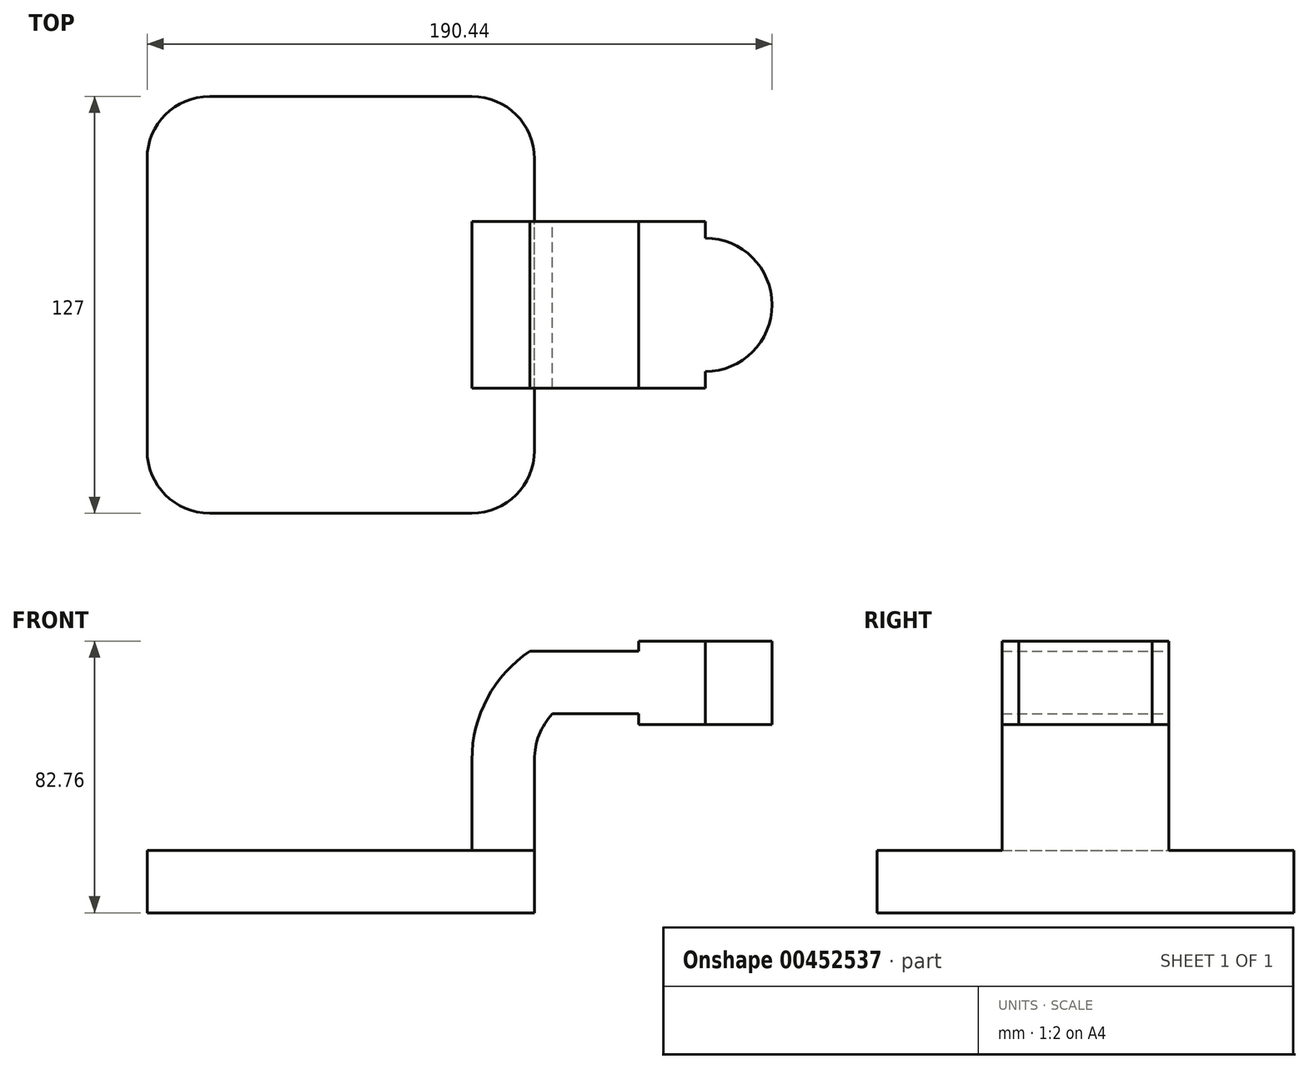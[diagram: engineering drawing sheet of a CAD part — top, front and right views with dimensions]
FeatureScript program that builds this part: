
annotation { "Feature Type Name" : "Feature", "Feature Type Description" : "" }
export const myFeature = defineFeature(function(context is Context, id is Id, definition is map)
    precondition{}
    {
        {
            var Q0;
            Q0=qCreatedBy(makeId("Front.planeOp"),FACE);
            var sketch = newSketch(context, id + "F0", { "sketchPlane" : qUnion([Q0])});
            skLineSegment(sketch, "E0.bottom", {"start": v(59.02, -9.52) * mm, "end": v(-59.02, -9.53) * mm});
            skLineSegment(sketch, "E0.top", {"start": v(59.02, 9.53) * mm, "end": v(-59.02, 9.53) * mm});
            skLineSegment(sketch, "E0.left", {"start": v(59.02, -9.52) * mm, "end": v(59.02, 9.53) * mm});
            skLineSegment(sketch, "E0.right", {"start": v(-59.02, -9.53) * mm, "end": v(-59.02, 9.53) * mm});
            skPoint(sketch, "E0.middle", {"position": v(0, 0) * mm});
            skLineSegment(sketch, "E1.bottom", {"start": v(131.42, 47.83) * mm, "end": v(90.78, 47.83) * mm});
            skLineSegment(sketch, "E1.top", {"start": v(131.42, 73.23) * mm, "end": v(90.78, 73.23) * mm});
            skLineSegment(sketch, "E1.left", {"start": v(131.42, 47.83) * mm, "end": v(131.42, 73.23) * mm});
            skLineSegment(sketch, "E1.right", {"start": v(90.78, 47.83) * mm, "end": v(90.78, 73.23) * mm});
            skPoint(sketch, "E1.middle", {"position": v(111.1, 60.53) * mm});
            skLineSegment(sketch, "E2", {"start": v(59.02, 9.53) * mm, "end": v(59.02, 37.13) * mm});
            skArc(sketch, "E3", {"start": v(59.02, 37.13) * mm, "mid": v(60.44, 44.63) * mm, "end": v(64.48, 51.1) * mm});
            skLineSegment(sketch, "E4", {"start": v(64.48, 51.1) * mm, "end": v(110.03, 51.1) * mm});
            skLineSegment(sketch, "E5.0", {"start": v(57.68, 70.15) * mm, "end": v(110.03, 70.15) * mm});
            skArc(sketch, "E5.1", {"start": v(39.97, 37.13) * mm, "mid": v(44.68, 55.87) * mm, "end": v(57.68, 70.15) * mm});
            skLineSegment(sketch, "E5.2", {"start": v(39.97, 9.53) * mm, "end": v(39.97, 37.13) * mm});
            skLineSegment(sketch, "E6", {"start": v(111.1, 47.83) * mm, "end": v(111.1, 73.23) * mm});
            skFitSpline(sketch, "E7", {"points": [v(-59.02, 9.52) * mm, v(57.68, 70.15) * mm], "startDerivative": vector(33.1, 114.92) * mm, "endDerivative": vector(257.8, 25.97) * mm});
            skSolve(sketch);
        }
        {
            var Q0;
            Q0=makeQuery(id+"F0.imprint","IMPRINT",FACE,{"disambiguationData":[TD([[makeQuery(id+"F0.imprint","IMPRINT",EDGE,{"derivedFrom":sQuery(id+"F0.wireOp",EDGE,"E0.bottom")}),-1.0]])]});
            extrude(context, id + "F1", {"entities" : qUnion([Q0]), "endBound" : BoundingType.SYMMETRIC, "depth" : 127 * mm});
        }
        {
            var Q0;
            {var subQ1=sQuery(id+"F0.wireOp",EDGE,"E2");Q0=makeQuery(id+"F0.imprint","IMPRINT",FACE,{"disambiguationData":[TD([[makeQuery(id+"F0.imprint","IMPRINT",EDGE,{"derivedFrom":subQ1}),1.0]])]});}
            var Q1;
            {var subQ0=sQuery(id+"F0.wireOp",EDGE,"E4");var subQ1=sQuery(id+"F0.wireOp",EDGE,"E1.right");var subQ2=makeQuery(id+"F0.imprint","INTERSECT",VERTEX,{"derivedFrom":[subQ1,subQ0]});Q1=makeQuery(id+"F0.imprint","IMPRINT",FACE,{"disambiguationData":[TD([[makeQuery(id+"F0.imprint","IMPRINT",EDGE,{"disambiguationData":[TD([[subQ2,-1.0]])],"derivedFrom":subQ1}),-1.0]])]});}
            extrude(context, id + "F2", {"entities" : qUnion([Q0, Q1]), "operationType" : NewBodyOperationType.ADD, "endBound" : BoundingType.SYMMETRIC, "depth" : 50.8 * mm});
        }
        {
            var Q0;
            Q0=makeQuery(id+"F0.imprint","IMPRINT",FACE,{"disambiguationData":[TD([[makeQuery(id+"F0.imprint","IMPRINT",EDGE,{"derivedFrom":sQuery(id+"F0.wireOp",EDGE,"E5.1")}),1.0]])]});
            extrude(context, id + "F3", {"entities" : qUnion([Q0]), "operationType" : NewBodyOperationType.ADD, "endBound" : BoundingType.SYMMETRIC, "depth" : 15.88 * mm});
        }
        {
            var Q0;
            Q0=makeQuery(id+"F1.opExtrude","CAP_EDGE",EDGE,{"disambiguationData":[OSD([sQuery(id+"F0.wireOp",EDGE,"E0.left")])],"isStart":false});
            var Q1;
            Q1=makeQuery(id+"F1.opExtrude","CAP_EDGE",EDGE,{"disambiguationData":[OSD([sQuery(id+"F0.wireOp",EDGE,"E0.right")])],"isStart":false});
            var Q2;
            Q2=makeQuery(id+"F1.opExtrude","CAP_EDGE",EDGE,{"disambiguationData":[OSD([sQuery(id+"F0.wireOp",EDGE,"E0.right")])],"isStart":true});
            var Q3;
            Q3=makeQuery(id+"F1.opExtrude","CAP_EDGE",EDGE,{"disambiguationData":[OSD([sQuery(id+"F0.wireOp",EDGE,"E0.left")])],"isStart":true});
            fillet(context, id + "F4", {"entities" : qUnion([Q0, Q1, Q2, Q3]), "radius" : 19.05 * mm, "tangentPropagation" : true, "allowEdgeOverflow" : false});
        }
        {
            var Q0;
            {var subQ0=sQuery(id+"F0.wireOp",EDGE,"E1.left");Q0=makeQuery(id+"F0.imprint","IMPRINT",FACE,{"disambiguationData":[TD([[makeQuery(id+"F0.imprint","IMPRINT",EDGE,{"derivedFrom":subQ0}),1.0]])]});}
            var Q1;
            Q1=sQuery(id+"F0.wireOp",EDGE,"E6");
            revolve(context, id + "F5", {"operationType" : NewBodyOperationType.ADD, "entities" : qUnion([Q0]), "axis" : qUnion([Q1]), "revolveType" : RevolveType.FULL});
        }
    });
